# Revit family: Prises non verrouillées saillies 100_130V
name_source: partatom
category: Installations électriques
revit_build: Autodesk Revit 2018 (Build: 20170223_1515(x64)
units: mm (PartAtom-declared; Revit-internal decimal feet)

## family parameters
Conserver l'orientation des annotations = Non
Cote de connecteur circulaire = Utiliser le diamètre
Couper avec des vides une fois chargée = Non
Hôte = Face
Partagée = Non
Point de calcul de pièce = Non
Type d'élément = Normal

## types (5) — shared parameters
Couleur caractéristique = jaune
Elévation par défaut = 1000 mm  [stored 3.28084 ft]
Fabricant = Legrand
Famille produit = 0854-P17 TEMPRA PRO
Position de la Terre h = 4
Prise au standard international pour montage encastré ou saillie avec accessoire permet la connexion d'appareils de puissance = Prise au standard international pour montage encastré ou saillie avec accessoire permet la connexion d'appareils de puissance
Standard CEI ou NFC = CEI
Température maximum d'utilisation = 40
Température minimum d'installation = -5
Température minimum d'utilisation = -25
Tension V = 110 V  50/60 Hz  jaune
Type de cerrouillage = x
matériau du boitier = plastique
résistance aux chocs IK = 9
type de raccordement = bornes à vis
zero-valued in all types: entraxe de fixation vertical mm

## per-type parameters (varying)
| type | Description | Diamètre entrée de câble | Intensité A | Modèle | Nombre de pôles | classe de protection IP | entraxe de fixation horizontal mm | hauteur mm | largeur mm | profondeur mm | sans halogène |
| IDS_LG_555151 | IDS_DESCRIPTION_LG_555151 | M20/M25 | 16 A | LG-555151 | 3 | IP44 | 70 mm | 131 mm  [stored 0.42979 ft] | 93 mm | 125 mm  [stored 0.410105 ft] | Oui |
| IDS_LG_555152 | IDS_DESCRIPTION_LG_555152 | M20/M25 | 16 A | LG-555152 | 4 | IP44 | 70 mm | 131 mm  [stored 0.42979 ft] | 93 mm | 133 mm  [stored 0.436352 ft] | Oui |
| IDS_LG_555251 | IDS_DESCRIPTION_LG_555251 | M25/M32 | 32 A | LG-555251 | 3 | IP44 | 90 mm | 156 mm  [stored 0.511811 ft] | 113 mm | 155 mm | Oui |
| IDS_LG_555351 | IDS_DESCRIPTION_LG_555351 | M20/M25 | 16 A | LG-555351 | 3 |  | 70 mm | 138 mm | 93 mm | 126 mm  [stored 0.413386 ft] | Non |
| IDS_LG_555451 | IDS_DESCRIPTION_LG_555451 | M25/M32 | 32 A | LG-555451 | 3 |  | 90 mm | 163 mm  [stored 0.534777 ft] | 113 mm | 156 mm  [stored 0.511811 ft] | Non |

note: [stored X ft] marks values corroborated as IEEE doubles in the binary element streams (Revit-internal decimal feet)
